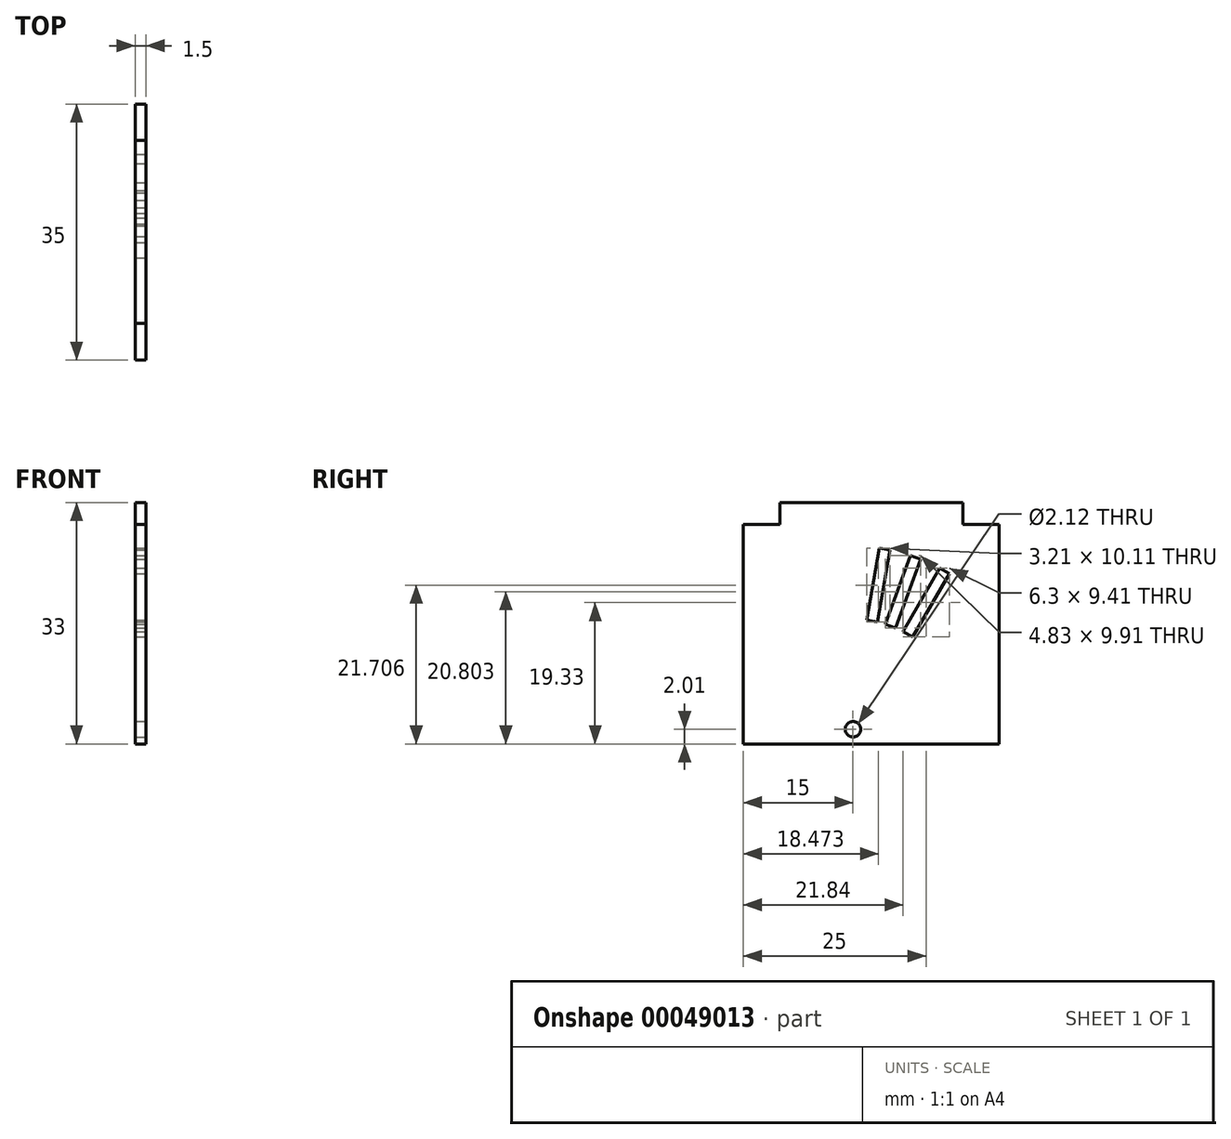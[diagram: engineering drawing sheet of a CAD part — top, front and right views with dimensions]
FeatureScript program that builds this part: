
annotation { "Feature Type Name" : "Feature", "Feature Type Description" : "" }
export const myFeature = defineFeature(function(context is Context, id is Id, definition is map)
    precondition{}
    {
        {
            var Q0;
            Q0=qCreatedBy(makeId("Right.planeOp"),FACE);
            var sketch = newSketch(context, id + "F0", { "sketchPlane" : qUnion([Q0])});
            skLineSegment(sketch, "E0.bottom", {"start": v(17.5, 15) * mm, "end": v(-17.5, 15) * mm});
            skLineSegment(sketch, "E0.top", {"start": v(17.5, -15) * mm, "end": v(-17.5, -15) * mm});
            skLineSegment(sketch, "E0.left", {"start": v(17.5, 15) * mm, "end": v(17.5, -15) * mm});
            skLineSegment(sketch, "E0.right", {"start": v(-17.5, 15) * mm, "end": v(-17.5, -15) * mm});
            skPoint(sketch, "E0.middle", {"position": v(0, 0) * mm});
            skSolve(sketch);
        }
        {
            var Q0;
            Q0 = qSketchRegion(id + "F0", true);
            extrude(context, id + "F1", {"entities" : qUnion([Q0]), "depth" : 1.5 * mm});
        }
        {
            var Q0;
            Q0=makeQuery(id+"F1.opExtrude","CAP_FACE",FACE,{"disambiguationData":[OSD([sQuery(id+"F0.wireOp",EDGE,"E0.bottom"),sQuery(id+"F0.wireOp",EDGE,"E0.top"),sQuery(id+"F0.wireOp",EDGE,"E0.left"),sQuery(id+"F0.wireOp",EDGE,"E0.right")])],"isStart":false});
            var sketch = newSketch(context, id + "F2", { "sketchPlane" : qUnion([Q0])});
            skLineSegment(sketch, "E1.bottom", {"start": v(-12.5, 15) * mm, "end": v(12.5, 15) * mm});
            skLineSegment(sketch, "E1.top", {"start": v(-12.5, 18) * mm, "end": v(12.5, 18) * mm});
            skLineSegment(sketch, "E1.left", {"start": v(-12.5, 15) * mm, "end": v(-12.5, 18) * mm});
            skLineSegment(sketch, "E1.right", {"start": v(12.5, 15) * mm, "end": v(12.5, 18) * mm});
            skLineSegment(sketch, "E2", {"start": v(-12.5, 15) * mm, "end": v(-17.5, 15) * mm, "construction": true});
            skLineSegment(sketch, "E3", {"start": v(12.5, 15) * mm, "end": v(17.5, 15) * mm, "construction": true});
            skSolve(sketch);
        }
        {
            var Q0;
            Q0 = qSketchRegion(id + "F2", true);
            extrude(context, id + "F3", {"entities" : qUnion([Q0]), "operationType" : NewBodyOperationType.ADD, "oppositeDirection" : true, "depth" : 1.5 * mm});
        }
        {
            var Q0;
            {var subQ0=sQuery(id+"F2.wireOp",EDGE,"E1.right");var subQ1=sQuery(id+"F2.wireOp",EDGE,"E1.left");var subQ2=sQuery(id+"F2.wireOp",EDGE,"E1.top");var subQ3=sQuery(id+"F2.wireOp",EDGE,"E1.bottom");Q0=makeQuery(id+"FjhHAxKVouPhXv1_1.1.F3.boolean.opBoolean","MERGE",FACE,{"derivedFrom":[makeQuery(id+"F3.boolean.opBoolean","MERGE",FACE,{"derivedFrom":[makeQuery(id+"F1.opExtrude","CAP_FACE",FACE,{"disambiguationData":[OSD([sQuery(id+"F0.wireOp",EDGE,"E0.bottom"),sQuery(id+"F0.wireOp",EDGE,"E0.top"),sQuery(id+"F0.wireOp",EDGE,"E0.left"),sQuery(id+"F0.wireOp",EDGE,"E0.right")])],"isStart":false}),makeQuery(id+"F3.opExtrude","CAP_FACE",FACE,{"disambiguationData":[OSD([subQ3,subQ2,subQ1,subQ0])],"isStart":true})]}),makeQuery(id+"FjhHAxKVouPhXv1_1.1.F3.opExtrude","CAP_FACE",FACE,{"disambiguationData":[OSD([subQ3,subQ2,subQ1,subQ0])],"isStart":true})]});}
            var sketch = newSketch(context, id + "F4", { "sketchPlane" : qUnion([Q0])});
            skLineSegment(sketch, "E4.bottom", {"start": v(-12.5, -18) * mm, "end": v(12.5, -18) * mm});
            skLineSegment(sketch, "E4.top", {"start": v(-12.5, -16.5) * mm, "end": v(12.5, -16.5) * mm});
            skLineSegment(sketch, "E4.left", {"start": v(-12.5, -18) * mm, "end": v(-12.5, -16.5) * mm});
            skLineSegment(sketch, "E4.right", {"start": v(12.5, -18) * mm, "end": v(12.5, -16.5) * mm});
            skSolve(sketch);
        }
        {
            var Q0;
            Q0 = qSketchRegion(id + "F4", true);
            extrude(context, id + "F5", {"entities" : qUnion([Q0]), "operationType" : NewBodyOperationType.REMOVE, "oppositeDirection" : true, "depth" : 25 * mm});
        }
        {
            var Q0;
            {var subQ0=sQuery(id+"F2.wireOp",EDGE,"E1.right");var subQ1=sQuery(id+"F2.wireOp",EDGE,"E1.left");var subQ2=sQuery(id+"F2.wireOp",EDGE,"E1.top");var subQ3=sQuery(id+"F2.wireOp",EDGE,"E1.bottom");Q0=makeQuery(id+"FjhHAxKVouPhXv1_1.1.F3.boolean.opBoolean","MERGE",FACE,{"derivedFrom":[makeQuery(id+"F3.boolean.opBoolean","MERGE",FACE,{"derivedFrom":[makeQuery(id+"F1.opExtrude","CAP_FACE",FACE,{"disambiguationData":[OSD([sQuery(id+"F0.wireOp",EDGE,"E0.bottom"),sQuery(id+"F0.wireOp",EDGE,"E0.top"),sQuery(id+"F0.wireOp",EDGE,"E0.left"),sQuery(id+"F0.wireOp",EDGE,"E0.right")])],"isStart":false}),makeQuery(id+"F3.opExtrude","CAP_FACE",FACE,{"disambiguationData":[OSD([subQ3,subQ2,subQ1,subQ0])],"isStart":true})]}),makeQuery(id+"FjhHAxKVouPhXv1_1.1.F3.opExtrude","CAP_FACE",FACE,{"disambiguationData":[OSD([subQ3,subQ2,subQ1,subQ0])],"isStart":true})]});}
            var sketch = newSketch(context, id + "F6", { "sketchPlane" : qUnion([Q0])});
            skLineSegment(sketch, "E5", {"start": v(-2.5, -13) * mm, "end": v(-2.5, 2) * mm, "construction": true});
            skLineSegment(sketch, "E6", {"start": v(-2.5, -13) * mm, "end": v(12.5, 13) * mm, "construction": true});
            skLineSegment(sketch, "E7", {"start": v(-2.5, -13) * mm, "end": v(7.76, 15.2) * mm, "construction": true});
            skLineSegment(sketch, "E8", {"start": v(-2.5, -13) * mm, "end": v(2.7, 16.55) * mm, "construction": true});
            skLineSegment(sketch, "E9", {"start": v(0.1, 1.78) * mm, "end": v(-0.63, 1.91) * mm});
            skLineSegment(sketch, "E10", {"start": v(-0.63, 1.91) * mm, "end": v(1.1, 11.76) * mm});
            skLineSegment(sketch, "E11", {"start": v(1.1, 11.76) * mm, "end": v(1.84, 11.63) * mm});
            skLineSegment(sketch, "E12", {"start": v(1.84, 11.63) * mm, "end": v(2.58, 11.5) * mm});
            skLineSegment(sketch, "E13", {"start": v(0.1, 1.78) * mm, "end": v(0.84, 1.65) * mm});
            skLineSegment(sketch, "E14", {"start": v(2.58, 11.5) * mm, "end": v(0.84, 1.65) * mm});
            skLineSegment(sketch, "E15.bottom", {"start": v(-3.25, -12.24) * mm, "end": v(-1.75, -12.24) * mm, "construction": true});
            skLineSegment(sketch, "E15.top", {"start": v(-3.25, -13.74) * mm, "end": v(-1.75, -13.74) * mm, "construction": true});
            skLineSegment(sketch, "E15.left", {"start": v(-3.25, -12.24) * mm, "end": v(-3.25, -13.74) * mm, "construction": true});
            skLineSegment(sketch, "E15.right", {"start": v(-1.75, -12.24) * mm, "end": v(-1.75, -13.74) * mm, "construction": true});
            skPoint(sketch, "E15.middle", {"position": v(-2.5, -13) * mm});
            skCircle(sketch, "E16", {"center": v(-2.5, -13) * mm, "radius": 1.06 * mm});
            skLineSegment(sketch, "E17", {"start": v(2.63, 1.1) * mm, "end": v(3.34, 0.85) * mm});
            skLineSegment(sketch, "E18", {"start": v(3.34, 0.85) * mm, "end": v(6.76, 10.25) * mm});
            skLineSegment(sketch, "E19", {"start": v(6.76, 10.25) * mm, "end": v(6.05, 10.5) * mm});
            skLineSegment(sketch, "E20", {"start": v(6.05, 10.5) * mm, "end": v(5.35, 10.76) * mm});
            skLineSegment(sketch, "E21", {"start": v(5.35, 10.76) * mm, "end": v(1.93, 1.36) * mm});
            skLineSegment(sketch, "E22", {"start": v(2.63, 1.1) * mm, "end": v(1.93, 1.36) * mm});
            skPoint(sketch, "E23.orphan", {"position": v(2.13, 1.91) * mm});
            skPoint(sketch, "E24.endSnap0", {"position": v(3.64, 6.06) * mm});
            skLineSegment(sketch, "E25", {"start": v(5, 0) * mm, "end": v(5.65, -0.38) * mm});
            skLineSegment(sketch, "E26", {"start": v(5.65, -0.38) * mm, "end": v(10.65, 8.29) * mm});
            skLineSegment(sketch, "E27", {"start": v(10.65, 8.29) * mm, "end": v(10, 8.66) * mm});
            skLineSegment(sketch, "E28", {"start": v(10, 8.66) * mm, "end": v(9.35, 9.04) * mm});
            skLineSegment(sketch, "E29", {"start": v(9.35, 9.04) * mm, "end": v(4.35, 0.37) * mm});
            skLineSegment(sketch, "E30", {"start": v(5, 0) * mm, "end": v(4.35, 0.37) * mm});
            skSolve(sketch);
        }
        {
            var Q0;
            Q0 = qSketchRegion(id + "F6", true);
            extrude(context, id + "F7", {"entities" : qUnion([Q0]), "operationType" : NewBodyOperationType.REMOVE, "endBound" : BoundingType.THROUGH_ALL, "oppositeDirection" : true, "depth" : 25 * mm});
        }
    });
